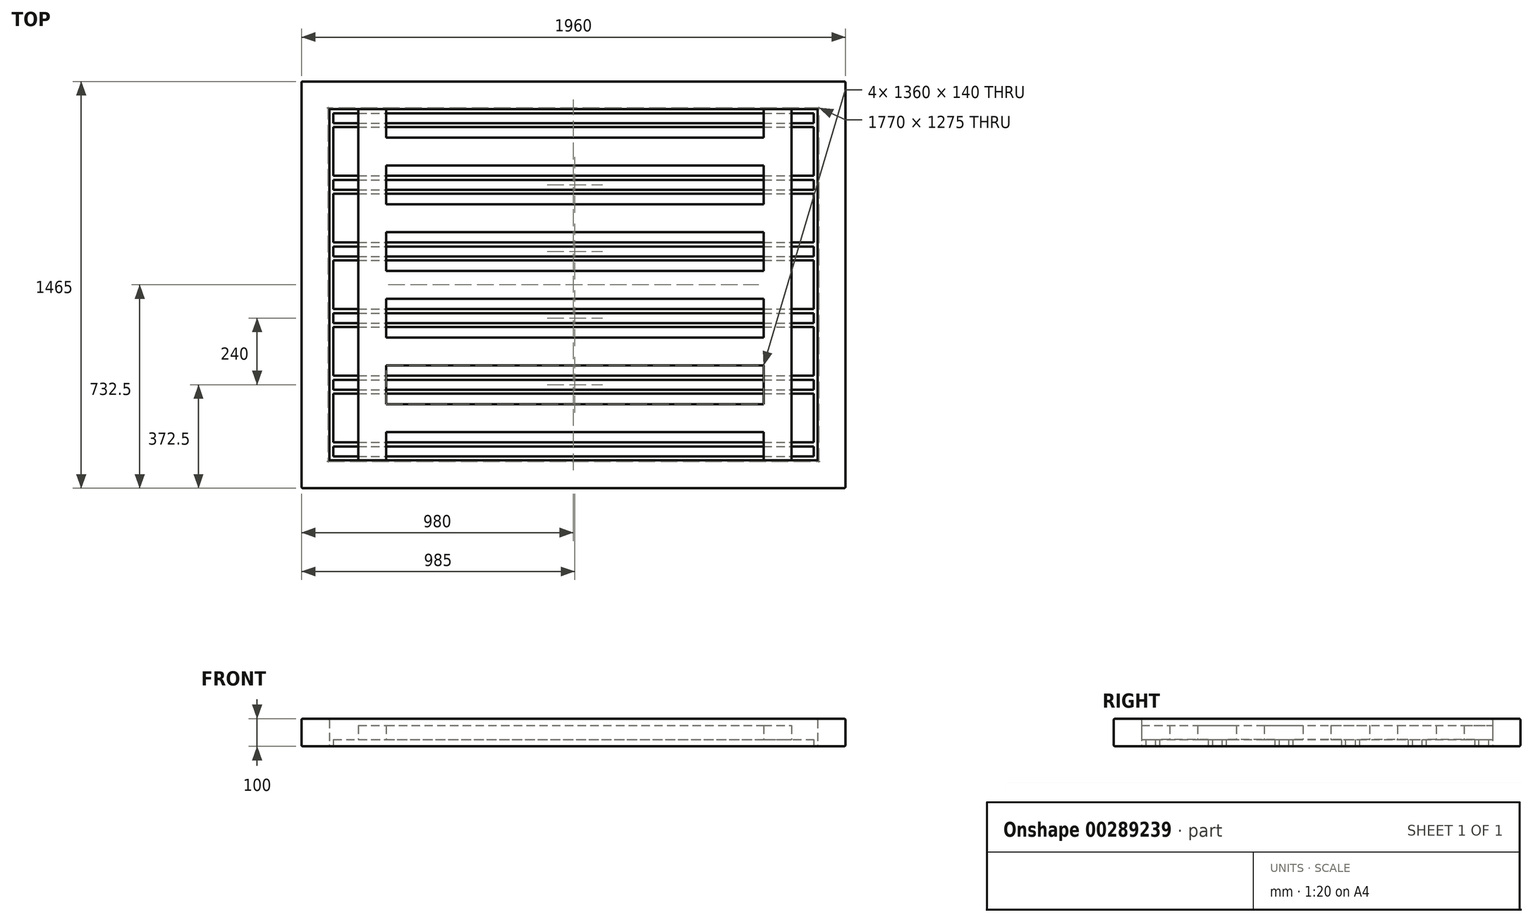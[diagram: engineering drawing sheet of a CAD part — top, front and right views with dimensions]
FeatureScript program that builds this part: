
annotation { "Feature Type Name" : "Feature", "Feature Type Description" : "" }
export const myFeature = defineFeature(function(context is Context, id is Id, definition is map)
    precondition{}
    {
        {
            var Q0;
            Q0=qCreatedBy(makeId("Top.planeOp"),FACE);
            var sketch = newSketch(context, id + "F0", { "sketchPlane" : qUnion([Q0])});
            skLineSegment(sketch, "E0.bottom", {"start": v(0, 0) * mm, "end": v(1960, 0) * mm});
            skLineSegment(sketch, "E0.top", {"start": v(0, 1465) * mm, "end": v(1960, 1465) * mm});
            skLineSegment(sketch, "E0.left", {"start": v(0, 0) * mm, "end": v(0, 1465) * mm});
            skLineSegment(sketch, "E0.right", {"start": v(1960, 0) * mm, "end": v(1960, 1465) * mm});
            skLineSegment(sketch, "E1.0", {"start": v(100, 1365) * mm, "end": v(1860, 1365) * mm});
            skLineSegment(sketch, "E1.1", {"start": v(100, 100) * mm, "end": v(100, 1365) * mm});
            skLineSegment(sketch, "E1.2", {"start": v(100, 100) * mm, "end": v(1860, 100) * mm});
            skLineSegment(sketch, "E1.3", {"start": v(1860, 100) * mm, "end": v(1860, 1365) * mm});
            skLineSegment(sketch, "E2.bottom", {"start": v(115, 115) * mm, "end": v(1845, 115) * mm});
            skLineSegment(sketch, "E2.top", {"start": v(115, 150) * mm, "end": v(1845, 150) * mm});
            skLineSegment(sketch, "E2.left", {"start": v(115, 115) * mm, "end": v(115, 150) * mm});
            skLineSegment(sketch, "E2.right", {"start": v(1845, 115) * mm, "end": v(1845, 150) * mm});
            skLineSegment(sketch, "E3.bottom", {"start": v(115, 340) * mm, "end": v(1845, 340) * mm});
            skLineSegment(sketch, "E3.top", {"start": v(115, 165) * mm, "end": v(1845, 165) * mm});
            skLineSegment(sketch, "E3.left", {"start": v(115, 340) * mm, "end": v(115, 165) * mm});
            skLineSegment(sketch, "E3.right", {"start": v(1845, 340) * mm, "end": v(1845, 165) * mm});
            skLineSegment(sketch, "E4.0.1.0", {"start": v(115, 580) * mm, "end": v(1845, 580) * mm});
            skLineSegment(sketch, "E4.0.1.1", {"start": v(1845, 580) * mm, "end": v(1845, 405) * mm});
            skLineSegment(sketch, "E4.0.1.2", {"start": v(115, 405) * mm, "end": v(1845, 405) * mm});
            skLineSegment(sketch, "E4.0.1.3", {"start": v(115, 580) * mm, "end": v(115, 405) * mm});
            skLineSegment(sketch, "E4.0.2.0", {"start": v(115, 820) * mm, "end": v(1845, 820) * mm});
            skLineSegment(sketch, "E4.0.2.1", {"start": v(1845, 820) * mm, "end": v(1845, 645) * mm});
            skLineSegment(sketch, "E4.0.2.2", {"start": v(115, 645) * mm, "end": v(1845, 645) * mm});
            skLineSegment(sketch, "E4.0.2.3", {"start": v(115, 820) * mm, "end": v(115, 645) * mm});
            skLineSegment(sketch, "E4.0.3.0", {"start": v(115, 1060) * mm, "end": v(1845, 1060) * mm});
            skLineSegment(sketch, "E4.0.3.1", {"start": v(1845, 1060) * mm, "end": v(1845, 885) * mm});
            skLineSegment(sketch, "E4.0.3.2", {"start": v(115, 885) * mm, "end": v(1845, 885) * mm});
            skLineSegment(sketch, "E4.0.3.3", {"start": v(115, 1060) * mm, "end": v(115, 885) * mm});
            skLineSegment(sketch, "E4.0.4.0", {"start": v(115, 1300) * mm, "end": v(1845, 1300) * mm});
            skLineSegment(sketch, "E4.0.4.1", {"start": v(1845, 1300) * mm, "end": v(1845, 1125) * mm});
            skLineSegment(sketch, "E4.0.4.2", {"start": v(115, 1125) * mm, "end": v(1845, 1125) * mm});
            skLineSegment(sketch, "E4.0.4.3", {"start": v(115, 1300) * mm, "end": v(115, 1125) * mm});
            skLineSegment(sketch, "E4.direction1", {"start": v(115, 165) * mm, "end": v(140, 165) * mm, "construction": true});
            skLineSegment(sketch, "E4.direction2", {"start": v(115, 165) * mm, "end": v(115, 405) * mm, "construction": true});
            skLineSegment(sketch, "E5.0.1.0", {"start": v(115, 355) * mm, "end": v(115, 390) * mm});
            skLineSegment(sketch, "E5.0.1.1", {"start": v(115, 390) * mm, "end": v(1845, 390) * mm});
            skLineSegment(sketch, "E5.0.1.2", {"start": v(115, 355) * mm, "end": v(1845, 355) * mm});
            skLineSegment(sketch, "E5.0.1.3", {"start": v(1845, 355) * mm, "end": v(1845, 390) * mm});
            skLineSegment(sketch, "E5.0.2.0", {"start": v(115, 595) * mm, "end": v(115, 630) * mm});
            skLineSegment(sketch, "E5.0.2.1", {"start": v(115, 630) * mm, "end": v(1845, 630) * mm});
            skLineSegment(sketch, "E5.0.2.2", {"start": v(115, 595) * mm, "end": v(1845, 595) * mm});
            skLineSegment(sketch, "E5.0.2.3", {"start": v(1845, 595) * mm, "end": v(1845, 630) * mm});
            skLineSegment(sketch, "E5.0.3.0", {"start": v(115, 835) * mm, "end": v(115, 870) * mm});
            skLineSegment(sketch, "E5.0.3.1", {"start": v(115, 870) * mm, "end": v(1845, 870) * mm});
            skLineSegment(sketch, "E5.0.3.2", {"start": v(115, 835) * mm, "end": v(1845, 835) * mm});
            skLineSegment(sketch, "E5.0.3.3", {"start": v(1845, 835) * mm, "end": v(1845, 870) * mm});
            skLineSegment(sketch, "E5.0.4.0", {"start": v(115, 1075) * mm, "end": v(115, 1110) * mm});
            skLineSegment(sketch, "E5.0.4.1", {"start": v(115, 1110) * mm, "end": v(1845, 1110) * mm});
            skLineSegment(sketch, "E5.0.4.2", {"start": v(115, 1075) * mm, "end": v(1845, 1075) * mm});
            skLineSegment(sketch, "E5.0.4.3", {"start": v(1845, 1075) * mm, "end": v(1845, 1110) * mm});
            skLineSegment(sketch, "E5.0.5.0", {"start": v(115, 1315) * mm, "end": v(115, 1350) * mm});
            skLineSegment(sketch, "E5.0.5.1", {"start": v(115, 1350) * mm, "end": v(1845, 1350) * mm});
            skLineSegment(sketch, "E5.0.5.2", {"start": v(115, 1315) * mm, "end": v(1845, 1315) * mm});
            skLineSegment(sketch, "E5.0.5.3", {"start": v(1845, 1315) * mm, "end": v(1845, 1350) * mm});
            skLineSegment(sketch, "E5.direction1", {"start": v(115, 115) * mm, "end": v(140, 115) * mm, "construction": true});
            skLineSegment(sketch, "E5.direction2", {"start": v(115, 115) * mm, "end": v(115, 355) * mm, "construction": true});
            skSolve(sketch);
        }
        {
            var Q0;
            Q0=makeQuery(id+"F0.imprint","IMPRINT",FACE,{"disambiguationData":[TD([[makeQuery(id+"F0.imprint","IMPRINT",EDGE,{"derivedFrom":sQuery(id+"F0.wireOp",EDGE,"E0.bottom")}),1.0]])]});
            extrude(context, id + "F1", {"entities" : qUnion([Q0]), "depth" : 100 * mm});
        }
        {
            var Q0;
            Q0 = qSketchRegion(id + "F0", true);
            var Q1;
            Q1=makeQuery(id+"F0.imprint","IMPRINT",FACE,{"disambiguationData":[TD([[makeQuery(id+"F0.imprint","IMPRINT",EDGE,{"derivedFrom":sQuery(id+"F0.wireOp",EDGE,"E4.0.4.0")}),-1.0]])]});
            var Q2;
            Q2=makeQuery(id+"F0.imprint","IMPRINT",FACE,{"disambiguationData":[TD([[makeQuery(id+"F0.imprint","IMPRINT",EDGE,{"derivedFrom":sQuery(id+"F0.wireOp",EDGE,"E4.0.3.0")}),-1.0]])]});
            var Q3;
            Q3=makeQuery(id+"F0.imprint","IMPRINT",FACE,{"disambiguationData":[TD([[makeQuery(id+"F0.imprint","IMPRINT",EDGE,{"derivedFrom":sQuery(id+"F0.wireOp",EDGE,"E4.0.2.0")}),-1.0]])]});
            var Q4;
            Q4=makeQuery(id+"F0.imprint","IMPRINT",FACE,{"disambiguationData":[TD([[makeQuery(id+"F0.imprint","IMPRINT",EDGE,{"derivedFrom":sQuery(id+"F0.wireOp",EDGE,"E4.0.1.0")}),-1.0]])]});
            var Q5;
            Q5=makeQuery(id+"F0.imprint","IMPRINT",FACE,{"disambiguationData":[TD([[makeQuery(id+"F0.imprint","IMPRINT",EDGE,{"derivedFrom":sQuery(id+"F0.wireOp",EDGE,"E3.bottom")}),-1.0]])]});
            var Q6;
            Q6=makeQuery(id+"F0.imprint","IMPRINT",FACE,{"disambiguationData":[TD([[makeQuery(id+"F0.imprint","IMPRINT",EDGE,{"derivedFrom":sQuery(id+"F0.wireOp",EDGE,"E2.bottom")}),1.0]])]});
            var Q7;
            Q7=makeQuery(id+"F0.imprint","IMPRINT",FACE,{"disambiguationData":[TD([[makeQuery(id+"F0.imprint","IMPRINT",EDGE,{"derivedFrom":sQuery(id+"F0.wireOp",EDGE,"1c48348b-8a3d-41b5-89dd-84f6cd14f65a.0.1.0")}),1.0]])]});
            var Q8;
            Q8=makeQuery(id+"F0.imprint","IMPRINT",FACE,{"disambiguationData":[TD([[makeQuery(id+"F0.imprint","IMPRINT",EDGE,{"derivedFrom":sQuery(id+"F0.wireOp",EDGE,"1c48348b-8a3d-41b5-89dd-84f6cd14f65a.0.2.0")}),1.0]])]});
            var Q9;
            Q9=makeQuery(id+"F0.imprint","IMPRINT",FACE,{"disambiguationData":[TD([[makeQuery(id+"F0.imprint","IMPRINT",EDGE,{"derivedFrom":sQuery(id+"F0.wireOp",EDGE,"1c48348b-8a3d-41b5-89dd-84f6cd14f65a.0.3.0")}),1.0]])]});
            var Q10;
            Q10=makeQuery(id+"F0.imprint","IMPRINT",FACE,{"disambiguationData":[TD([[makeQuery(id+"F0.imprint","IMPRINT",EDGE,{"derivedFrom":sQuery(id+"F0.wireOp",EDGE,"1c48348b-8a3d-41b5-89dd-84f6cd14f65a.0.4.0")}),1.0]])]});
            var Q11;
            Q11=makeQuery(id+"F0.imprint","IMPRINT",FACE,{"disambiguationData":[TD([[makeQuery(id+"F0.imprint","IMPRINT",EDGE,{"derivedFrom":sQuery(id+"F0.wireOp",EDGE,"1c48348b-8a3d-41b5-89dd-84f6cd14f65a.0.5.0")}),1.0]])]});
            var Q12;
            Q12=makeQuery(id+"F0.imprint","IMPRINT",FACE,{"disambiguationData":[TD([[makeQuery(id+"F0.imprint","IMPRINT",EDGE,{"derivedFrom":sQuery(id+"F0.wireOp",EDGE,"E5.0.1.0")}),-1.0]])]});
            var Q13;
            Q13=makeQuery(id+"F0.imprint","IMPRINT",FACE,{"disambiguationData":[TD([[makeQuery(id+"F0.imprint","IMPRINT",EDGE,{"derivedFrom":sQuery(id+"F0.wireOp",EDGE,"E5.0.2.0")}),-1.0]])]});
            var Q14;
            Q14=makeQuery(id+"F0.imprint","IMPRINT",FACE,{"disambiguationData":[TD([[makeQuery(id+"F0.imprint","IMPRINT",EDGE,{"derivedFrom":sQuery(id+"F0.wireOp",EDGE,"E5.0.3.0")}),-1.0]])]});
            var Q15;
            Q15=makeQuery(id+"F0.imprint","IMPRINT",FACE,{"disambiguationData":[TD([[makeQuery(id+"F0.imprint","IMPRINT",EDGE,{"derivedFrom":sQuery(id+"F0.wireOp",EDGE,"E5.0.4.0")}),-1.0]])]});
            var Q16;
            Q16=makeQuery(id+"F0.imprint","IMPRINT",FACE,{"disambiguationData":[TD([[makeQuery(id+"F0.imprint","IMPRINT",EDGE,{"derivedFrom":sQuery(id+"F0.wireOp",EDGE,"E5.0.5.0")}),-1.0]])]});
            extrude(context, id + "F2", {"entities" : qUnion([Q0, Q1, Q2, Q3, Q4, Q5, Q6, Q7, Q8, Q9, Q10, Q11, Q12, Q13, Q14, Q15, Q16]), "operationType" : NewBodyOperationType.ADD, "depth" : 25 * mm});
        }
        {
            var Q0;
            Q0=makeQuery(id+"F1.opExtrude","CAP_EDGE",EDGE,{"disambiguationData":[OSD([sQuery(id+"F0.wireOp",EDGE,"E1.0")])],"isStart":false});
            var Q1;
            Q1=makeQuery(id+"F1.opExtrude","CAP_EDGE",EDGE,{"disambiguationData":[OSD([sQuery(id+"F0.wireOp",EDGE,"E1.1")])],"isStart":false});
            var Q2;
            Q2=makeQuery(id+"F1.opExtrude","CAP_EDGE",EDGE,{"disambiguationData":[OSD([sQuery(id+"F0.wireOp",EDGE,"E1.2")])],"isStart":false});
            var Q3;
            Q3=makeQuery(id+"F1.opExtrude","CAP_EDGE",EDGE,{"disambiguationData":[OSD([sQuery(id+"F0.wireOp",EDGE,"E1.3")])],"isStart":false});
            fillet(context, id + "F3", {"entities" : qUnion([Q0, Q1, Q2, Q3]), "radius" : 5 * mm, "tangentPropagation" : true, "allowEdgeOverflow" : false});
        }
        {
            var Q0;
            Q0=makeQuery(id+"F1.opExtrude","CAP_EDGE",EDGE,{"disambiguationData":[OSD([sQuery(id+"F0.wireOp",EDGE,"E0.top")])],"isStart":false});
            var Q1;
            Q1=makeQuery(id+"F1.opExtrude","CAP_EDGE",EDGE,{"disambiguationData":[OSD([sQuery(id+"F0.wireOp",EDGE,"E0.left")])],"isStart":false});
            var Q2;
            Q2=makeQuery(id+"F1.opExtrude","CAP_EDGE",EDGE,{"disambiguationData":[OSD([sQuery(id+"F0.wireOp",EDGE,"E0.right")])],"isStart":false});
            var Q3;
            Q3=makeQuery(id+"F1.opExtrude","CAP_EDGE",EDGE,{"disambiguationData":[OSD([sQuery(id+"F0.wireOp",EDGE,"E0.bottom")])],"isStart":false});
            var Q4;
            Q4=makeQuery(id+"F1.opExtrude","SWEPT_EDGE",EDGE,{"disambiguationData":[OSD([sQuery(id+"F0.wireOp",EDGE,"E0.bottom"),sQuery(id+"F0.wireOp",EDGE,"E0.right")])]});
            var Q5;
            Q5=makeQuery(id+"F1.opExtrude","SWEPT_EDGE",EDGE,{"disambiguationData":[OSD([sQuery(id+"F0.wireOp",EDGE,"E0.bottom"),sQuery(id+"F0.wireOp",EDGE,"E0.left")])]});
            var Q6;
            Q6=makeQuery(id+"F1.opExtrude","CAP_EDGE",EDGE,{"disambiguationData":[OSD([sQuery(id+"F0.wireOp",EDGE,"E0.bottom")])],"isStart":true});
            var Q7;
            Q7=makeQuery(id+"F1.opExtrude","CAP_EDGE",EDGE,{"disambiguationData":[OSD([sQuery(id+"F0.wireOp",EDGE,"E0.left")])],"isStart":true});
            var Q8;
            Q8=makeQuery(id+"F1.opExtrude","SWEPT_EDGE",EDGE,{"disambiguationData":[OSD([sQuery(id+"F0.wireOp",EDGE,"E0.top"),sQuery(id+"F0.wireOp",EDGE,"E0.left")])]});
            var Q9;
            Q9=makeQuery(id+"F1.opExtrude","CAP_EDGE",EDGE,{"disambiguationData":[OSD([sQuery(id+"F0.wireOp",EDGE,"E0.top")])],"isStart":true});
            var Q10;
            Q10=makeQuery(id+"F1.opExtrude","SWEPT_EDGE",EDGE,{"disambiguationData":[OSD([sQuery(id+"F0.wireOp",EDGE,"E0.top"),sQuery(id+"F0.wireOp",EDGE,"E0.right")])]});
            var Q11;
            Q11=makeQuery(id+"F1.opExtrude","CAP_EDGE",EDGE,{"disambiguationData":[OSD([sQuery(id+"F0.wireOp",EDGE,"E0.right")])],"isStart":true});
            var Q12;
            Q12=makeQuery(id+"F1.opExtrude","CAP_EDGE",EDGE,{"disambiguationData":[OSD([sQuery(id+"F0.wireOp",EDGE,"E1.1")])],"isStart":true});
            var Q13;
            Q13=makeQuery(id+"F1.opExtrude","CAP_EDGE",EDGE,{"disambiguationData":[OSD([sQuery(id+"F0.wireOp",EDGE,"E1.0")])],"isStart":true});
            var Q14;
            Q14=makeQuery(id+"F1.opExtrude","CAP_EDGE",EDGE,{"disambiguationData":[OSD([sQuery(id+"F0.wireOp",EDGE,"E1.2")])],"isStart":true});
            var Q15;
            Q15=makeQuery(id+"F1.opExtrude","CAP_EDGE",EDGE,{"disambiguationData":[OSD([sQuery(id+"F0.wireOp",EDGE,"E1.3")])],"isStart":true});
            fillet(context, id + "F4", {"entities" : qUnion([Q0, Q1, Q2, Q3, Q4, Q5, Q6, Q7, Q8, Q9, Q10, Q11, Q12, Q13, Q14, Q15]), "radius" : 5 * mm, "tangentPropagation" : true, "allowEdgeOverflow" : false});
        }
        {
            var Q0;
            Q0=makeQuery(id+"F2.opExtrude","CAP_FACE",FACE,{"disambiguationData":[OSD([sQuery(id+"F0.wireOp",EDGE,"E4.0.4.0"),sQuery(id+"F0.wireOp",EDGE,"E4.0.4.1"),sQuery(id+"F0.wireOp",EDGE,"E4.0.4.2"),sQuery(id+"F0.wireOp",EDGE,"E4.0.4.3")])],"isStart":false});
            var sketch = newSketch(context, id + "F5", { "sketchPlane" : qUnion([Q0])});
            skLineSegment(sketch, "E6.bottom", {"start": v(205, 100) * mm, "end": v(305, 100) * mm});
            skLineSegment(sketch, "E6.top", {"start": v(205, 1365) * mm, "end": v(305, 1365) * mm});
            skLineSegment(sketch, "E6.left", {"start": v(205, 100) * mm, "end": v(205, 1365) * mm});
            skLineSegment(sketch, "E6.right", {"start": v(305, 100) * mm, "end": v(305, 202.5) * mm});
            skLineSegment(sketch, "E7.1.0.0", {"start": v(1665, 100) * mm, "end": v(1665, 202.5) * mm});
            skLineSegment(sketch, "E7.1.0.1", {"start": v(1665, 1365) * mm, "end": v(1765, 1365) * mm});
            skLineSegment(sketch, "E7.1.0.2", {"start": v(1765, 100) * mm, "end": v(1765, 1365) * mm});
            skLineSegment(sketch, "E7.1.0.3", {"start": v(1665, 100) * mm, "end": v(1765, 100) * mm});
            skLineSegment(sketch, "E7.direction1", {"start": v(205, 100) * mm, "end": v(1665, 100) * mm, "construction": true});
            skLineSegment(sketch, "E8.bottom", {"start": v(305, 202.5) * mm, "end": v(1665, 202.5) * mm});
            skLineSegment(sketch, "E8.top", {"start": v(305, 302.5) * mm, "end": v(1665, 302.5) * mm});
            skLineSegment(sketch, "E9.trimOffspring", {"start": v(305, 302.5) * mm, "end": v(305, 442.5) * mm});
            skLineSegment(sketch, "E10.trimOffspring", {"start": v(1665, 302.5) * mm, "end": v(1665, 442.5) * mm});
            skLineSegment(sketch, "E11.0.1.0", {"start": v(305, 442.5) * mm, "end": v(1665, 442.5) * mm});
            skLineSegment(sketch, "E11.0.1.1", {"start": v(305, 542.5) * mm, "end": v(1665, 542.5) * mm});
            skLineSegment(sketch, "E11.0.2.0", {"start": v(305, 682.5) * mm, "end": v(1665, 682.5) * mm});
            skLineSegment(sketch, "E11.0.2.1", {"start": v(305, 782.5) * mm, "end": v(1665, 782.5) * mm});
            skLineSegment(sketch, "E11.0.3.0", {"start": v(305, 922.5) * mm, "end": v(1665, 922.5) * mm});
            skLineSegment(sketch, "E11.0.3.1", {"start": v(305, 1022.5) * mm, "end": v(1665, 1022.5) * mm});
            skLineSegment(sketch, "E11.0.4.0", {"start": v(305, 1162.5) * mm, "end": v(1665, 1162.5) * mm});
            skLineSegment(sketch, "E11.0.4.1", {"start": v(305, 1262.5) * mm, "end": v(1665, 1262.5) * mm});
            skLineSegment(sketch, "E11.direction1", {"start": v(305, 202.5) * mm, "end": v(330, 202.5) * mm, "construction": true});
            skLineSegment(sketch, "E11.direction2", {"start": v(305, 202.5) * mm, "end": v(305, 442.5) * mm, "construction": true});
            skLineSegment(sketch, "E12.trimOffspring", {"start": v(305, 542.5) * mm, "end": v(305, 682.5) * mm});
            skLineSegment(sketch, "E13.trimOffspring", {"start": v(305, 782.5) * mm, "end": v(305, 922.5) * mm});
            skLineSegment(sketch, "E14.trimOffspring", {"start": v(305, 1022.5) * mm, "end": v(305, 1162.5) * mm});
            skLineSegment(sketch, "E15.trimOffspring", {"start": v(305, 1262.5) * mm, "end": v(305, 1365) * mm});
            skLineSegment(sketch, "E16.trimOffspring", {"start": v(1665, 1262.5) * mm, "end": v(1665, 1365) * mm});
            skLineSegment(sketch, "E17.trimOffspring", {"start": v(1665, 1022.5) * mm, "end": v(1665, 1162.5) * mm});
            skLineSegment(sketch, "E18.trimOffspring", {"start": v(1665, 782.5) * mm, "end": v(1665, 922.5) * mm});
            skLineSegment(sketch, "E19.trimOffspring", {"start": v(1665, 542.5) * mm, "end": v(1665, 682.5) * mm});
            skSolve(sketch);
        }
        {
            var Q0;
            Q0 = qSketchRegion(id + "F5", true);
            extrude(context, id + "F6", {"entities" : qUnion([Q0]), "depth" : 50 * mm});
        }
    });
